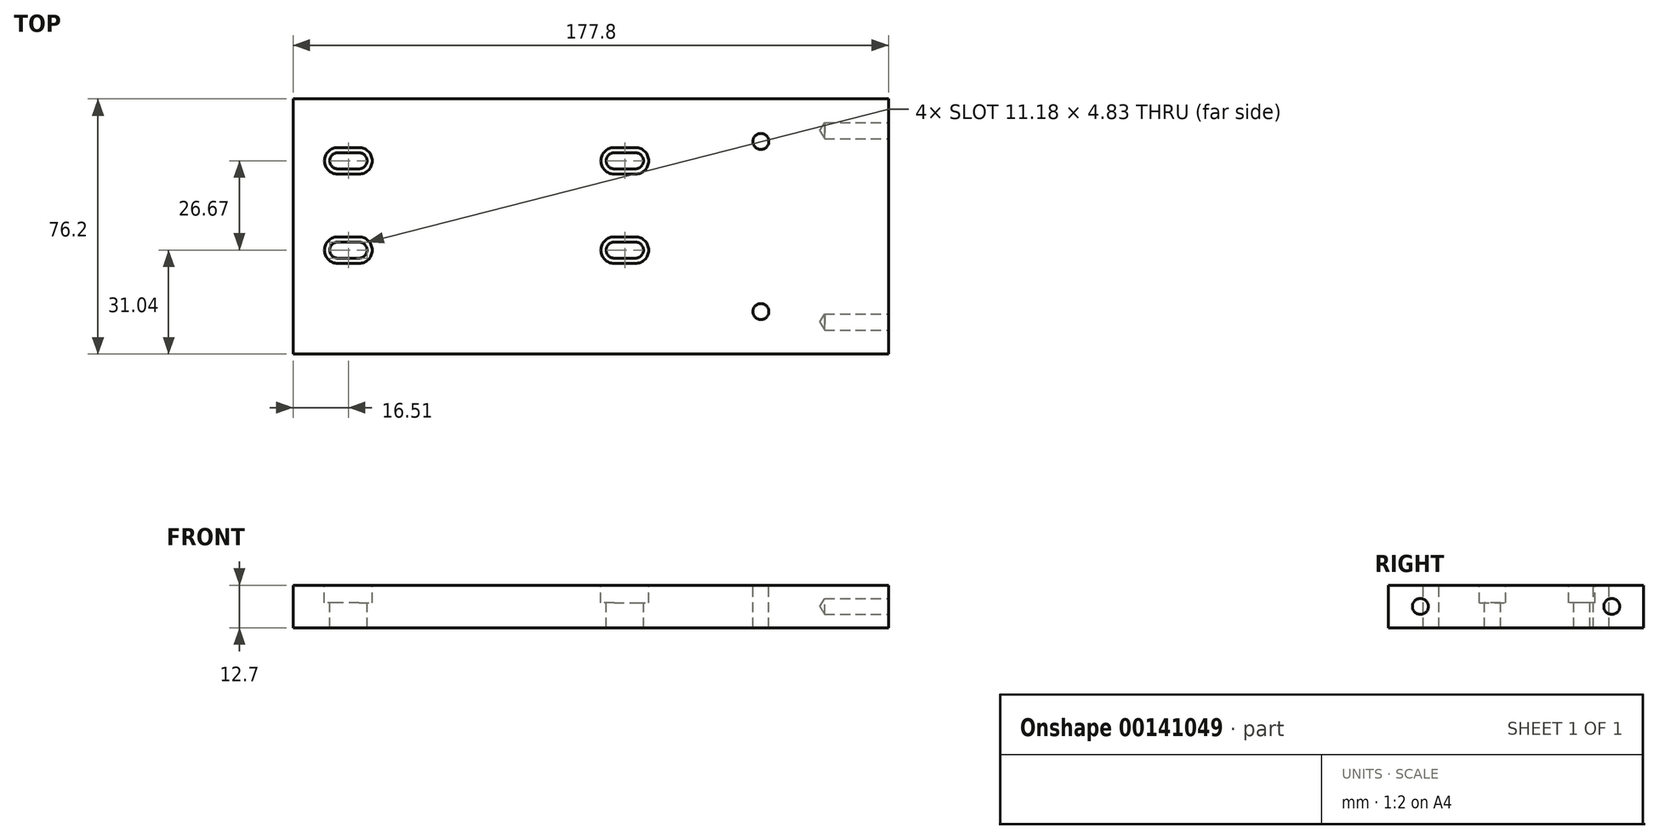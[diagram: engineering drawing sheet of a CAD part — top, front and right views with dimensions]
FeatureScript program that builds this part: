
annotation { "Feature Type Name" : "Feature", "Feature Type Description" : "" }
export const myFeature = defineFeature(function(context is Context, id is Id, definition is map)
    precondition{}
    {
        {
            var Q0;
            Q0=qCreatedBy(makeId("Top.planeOp"),FACE);
            var sketch = newSketch(context, id + "F0", { "sketchPlane" : qUnion([Q0])});
            skLineSegment(sketch, "E0.bottom", {"start": v(-62.23, 18.5) * mm, "end": v(115.57, 18.5) * mm});
            skLineSegment(sketch, "E0.top", {"start": v(-62.23, -57.7) * mm, "end": v(115.57, -57.7) * mm});
            skLineSegment(sketch, "E0.left", {"start": v(-62.23, 18.5) * mm, "end": v(-62.23, -57.7) * mm});
            skLineSegment(sketch, "E0.right", {"start": v(115.57, 18.5) * mm, "end": v(115.57, -57.7) * mm});
            skArc(sketch, "E1", {"start": v(-48.9, 2.41) * mm, "mid": v(-51.3, 0) * mm, "end": v(-48.9, -2.41) * mm});
            skArc(sketch, "E2", {"start": v(-42.55, -2.41) * mm, "mid": v(-40.13, 0) * mm, "end": v(-42.55, 2.41) * mm});
            skLineSegment(sketch, "E3", {"start": v(-48.9, 2.41) * mm, "end": v(-42.55, 2.41) * mm});
            skLineSegment(sketch, "E4", {"start": v(-48.9, -2.41) * mm, "end": v(-42.55, -2.41) * mm});
            skLineSegment(sketch, "E5", {"start": v(-4.45, -6.54) * mm, "end": v(-4.45, -13.34) * mm});
            skArc(sketch, "E6.MirrorCS", {"start": v(33.65, -2.41) * mm, "mid": v(31.24, 0) * mm, "end": v(33.66, 2.41) * mm});
            skLineSegment(sketch, "E7.MirrorCS", {"start": v(40, 2.41) * mm, "end": v(33.66, 2.41) * mm});
            skArc(sketch, "E8.MirrorCS", {"start": v(40, 2.41) * mm, "mid": v(42.42, 0) * mm, "end": v(40, -2.41) * mm});
            skLineSegment(sketch, "E9.MirrorCS", {"start": v(40, -2.41) * mm, "end": v(33.65, -2.41) * mm});
            skLineSegment(sketch, "E10", {"start": v(-4.45, -13.34) * mm, "end": v(-16.04, -13.34) * mm});
            skLineSegment(sketch, "E11.MirrorCS", {"start": v(-48.9, -24.26) * mm, "end": v(-42.55, -24.26) * mm});
            skArc(sketch, "E12.MirrorCS", {"start": v(-42.55, -24.26) * mm, "mid": v(-40.13, -26.67) * mm, "end": v(-42.55, -29.08) * mm});
            skLineSegment(sketch, "E13.MirrorCS", {"start": v(-48.9, -29.08) * mm, "end": v(-42.55, -29.08) * mm});
            skArc(sketch, "E14.MirrorCS", {"start": v(-48.9, -29.08) * mm, "mid": v(-51.3, -26.67) * mm, "end": v(-48.9, -24.26) * mm});
            skArc(sketch, "E15.MirrorCS", {"start": v(33.65, -24.26) * mm, "mid": v(31.24, -26.67) * mm, "end": v(33.66, -29.08) * mm});
            skLineSegment(sketch, "E16.MirrorCS", {"start": v(40, -24.26) * mm, "end": v(33.65, -24.26) * mm});
            skArc(sketch, "E17.MirrorCS", {"start": v(40, -29.08) * mm, "mid": v(42.42, -26.67) * mm, "end": v(40, -24.26) * mm});
            skLineSegment(sketch, "E18.MirrorCS", {"start": v(40, -29.08) * mm, "end": v(33.66, -29.08) * mm});
            skCircle(sketch, "E19", {"center": v(77.47, -45) * mm, "radius": 2.39 * mm});
            skCircle(sketch, "E20", {"center": v(77.47, 5.8) * mm, "radius": 2.39 * mm});
            skSolve(sketch);
        }
        {
            var Q0;
            Q0 = qSketchRegion(id + "F0", true);
            extrude(context, id + "F1", {"entities" : qUnion([Q0]), "oppositeDirection" : true, "depth" : 12.7 * mm});
        }
        {
            var Q0;
            Q0=makeQuery(id+"F1.opExtrude","CAP_FACE",FACE,{"disambiguationData":[OSD([sQuery(id+"F0.wireOp",EDGE,"E0.bottom"),sQuery(id+"F0.wireOp",EDGE,"E0.top"),sQuery(id+"F0.wireOp",EDGE,"E0.left"),sQuery(id+"F0.wireOp",EDGE,"E0.right"),sQuery(id+"F0.wireOp",EDGE,"E1"),sQuery(id+"F0.wireOp",EDGE,"E2"),sQuery(id+"F0.wireOp",EDGE,"E3"),sQuery(id+"F0.wireOp",EDGE,"E4"),sQuery(id+"F0.wireOp",EDGE,"E6.MirrorCS"),sQuery(id+"F0.wireOp",EDGE,"E7.MirrorCS"),sQuery(id+"F0.wireOp",EDGE,"E8.MirrorCS"),sQuery(id+"F0.wireOp",EDGE,"E9.MirrorCS"),sQuery(id+"F0.wireOp",EDGE,"E11.MirrorCS"),sQuery(id+"F0.wireOp",EDGE,"E12.MirrorCS"),sQuery(id+"F0.wireOp",EDGE,"E13.MirrorCS"),sQuery(id+"F0.wireOp",EDGE,"E14.MirrorCS"),sQuery(id+"F0.wireOp",EDGE,"E15.MirrorCS"),sQuery(id+"F0.wireOp",EDGE,"E16.MirrorCS"),sQuery(id+"F0.wireOp",EDGE,"E17.MirrorCS"),sQuery(id+"F0.wireOp",EDGE,"E18.MirrorCS"),sQuery(id+"F0.wireOp",EDGE,"E19"),sQuery(id+"F0.wireOp",EDGE,"E20")])],"isStart":true});
            var sketch = newSketch(context, id + "F2", { "sketchPlane" : qUnion([Q0])});
            skArc(sketch, "E21", {"start": v(-48.9, 3.96) * mm, "mid": v(-52.86, 0) * mm, "end": v(-48.9, -3.96) * mm});
            skLineSegment(sketch, "E22", {"start": v(-48.9, 3.96) * mm, "end": v(-42.55, 3.96) * mm});
            skLineSegment(sketch, "E23", {"start": v(-48.9, -3.96) * mm, "end": v(-42.55, -3.96) * mm});
            skArc(sketch, "E24.trimOffspring", {"start": v(-42.55, -3.96) * mm, "mid": v(-38.58, 0) * mm, "end": v(-42.55, 3.96) * mm});
            skLineSegment(sketch, "E25", {"start": v(-4.45, -5.1) * mm, "end": v(-4.45, -16.8) * mm});
            skLineSegment(sketch, "E26", {"start": v(-23.98, -13.34) * mm, "end": v(-14.32, -13.34) * mm});
            skLineSegment(sketch, "E27.MirrorCS", {"start": v(40, -3.96) * mm, "end": v(33.65, -3.96) * mm});
            skArc(sketch, "E28.MirrorCS", {"start": v(33.65, -3.96) * mm, "mid": v(29.7, 0) * mm, "end": v(33.65, 3.96) * mm});
            skLineSegment(sketch, "E29.MirrorCS", {"start": v(40, 3.96) * mm, "end": v(33.65, 3.96) * mm});
            skArc(sketch, "E30.MirrorCS", {"start": v(40, 3.96) * mm, "mid": v(43.97, 0) * mm, "end": v(40, -3.96) * mm});
            skLineSegment(sketch, "E31.MirrorCS", {"start": v(40, -22.7) * mm, "end": v(33.66, -22.7) * mm});
            skArc(sketch, "E32.MirrorCS", {"start": v(40, -30.63) * mm, "mid": v(43.97, -26.67) * mm, "end": v(40, -22.7) * mm});
            skLineSegment(sketch, "E33.MirrorCS", {"start": v(40, -30.63) * mm, "end": v(33.66, -30.63) * mm});
            skArc(sketch, "E34.MirrorCS", {"start": v(33.66, -22.7) * mm, "mid": v(29.7, -26.67) * mm, "end": v(33.66, -30.63) * mm});
            skLineSegment(sketch, "E35.MirrorCS", {"start": v(-48.9, -22.7) * mm, "end": v(-42.55, -22.7) * mm});
            skArc(sketch, "E36.MirrorCS", {"start": v(-42.55, -22.7) * mm, "mid": v(-38.58, -26.67) * mm, "end": v(-42.55, -30.63) * mm});
            skLineSegment(sketch, "E37.MirrorCS", {"start": v(-48.9, -30.63) * mm, "end": v(-42.55, -30.63) * mm});
            skArc(sketch, "E38.MirrorCS", {"start": v(-48.9, -30.63) * mm, "mid": v(-52.86, -26.67) * mm, "end": v(-48.9, -22.7) * mm});
            skSolve(sketch);
        }
        {
            var Q0;
            Q0 = qSketchRegion(id + "F2", true);
            extrude(context, id + "F3", {"entities" : qUnion([Q0]), "operationType" : NewBodyOperationType.REMOVE, "oppositeDirection" : true, "depth" : 5.2 * mm});
        }
        {
            var Q0;
            Q0=makeQuery(id+"F1.opExtrude","SWEPT_FACE",FACE,{"disambiguationData":[OSD([sQuery(id+"F0.wireOp",EDGE,"E0.right")])]});
            var sketch = newSketch(context, id + "F4", { "sketchPlane" : qUnion([Q0])});
            skCircle(sketch, "E39", {"center": v(-48.18, -6.35) * mm, "radius": 2.39 * mm});
            skPoint(sketch, "E39.centerSnap0", {"position": v(-57.7, -6.35) * mm});
            skCircle(sketch, "E40", {"center": v(8.97, -6.35) * mm, "radius": 2.39 * mm});
            skSolve(sketch);
        }
        {
            var Q0;
            Q0=sQuery(id+"F4.wireOp",VERTEX,"E39.center");
            var Q1;
            Q1=sQuery(id+"F4.wireOp",VERTEX,"E40.center");
            var Q2;
            Q2=makeQuery(id+"F1.opExtrude","SWEPT_BODY",BODY,{"disambiguationData":[OSD([sQuery(id+"F0.wireOp",EDGE,"E0.bottom"),sQuery(id+"F0.wireOp",EDGE,"E0.top"),sQuery(id+"F0.wireOp",EDGE,"E0.left"),sQuery(id+"F0.wireOp",EDGE,"E0.right"),sQuery(id+"F0.wireOp",EDGE,"E1"),sQuery(id+"F0.wireOp",EDGE,"E2"),sQuery(id+"F0.wireOp",EDGE,"E3"),sQuery(id+"F0.wireOp",EDGE,"E4"),sQuery(id+"F0.wireOp",EDGE,"E6.MirrorCS"),sQuery(id+"F0.wireOp",EDGE,"E7.MirrorCS"),sQuery(id+"F0.wireOp",EDGE,"E8.MirrorCS"),sQuery(id+"F0.wireOp",EDGE,"E9.MirrorCS"),sQuery(id+"F0.wireOp",EDGE,"E11.MirrorCS"),sQuery(id+"F0.wireOp",EDGE,"E12.MirrorCS"),sQuery(id+"F0.wireOp",EDGE,"E13.MirrorCS"),sQuery(id+"F0.wireOp",EDGE,"E14.MirrorCS"),sQuery(id+"F0.wireOp",EDGE,"E15.MirrorCS"),sQuery(id+"F0.wireOp",EDGE,"E16.MirrorCS"),sQuery(id+"F0.wireOp",EDGE,"E17.MirrorCS"),sQuery(id+"F0.wireOp",EDGE,"E18.MirrorCS"),sQuery(id+"F0.wireOp",EDGE,"E19"),sQuery(id+"F0.wireOp",EDGE,"E20")])]});
            hole(context, id + "F5", {"style" : HoleStyle.SIMPLE, "endStyle" : HoleEndStyle.BLIND, "holeDiameter" : 4.78 * mm, "holeDepth" : 19.05 * mm, "locations" : qUnion([Q0, Q1]), "scope" : qUnion([Q2])});
        }
    });
